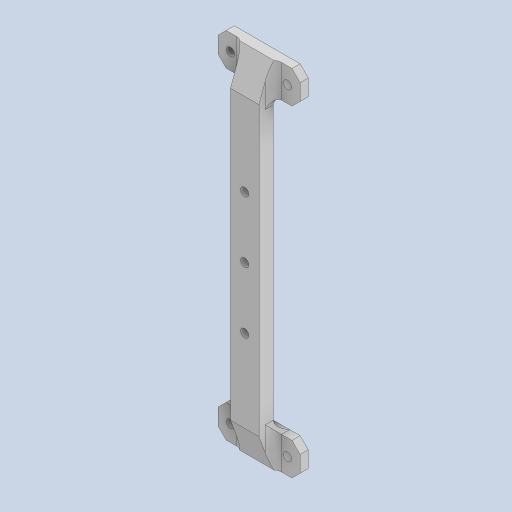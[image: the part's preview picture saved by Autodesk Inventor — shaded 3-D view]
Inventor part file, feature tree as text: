
AUTODESK INVENTOR PART (.ipt)
format: ipt  version: 2023 (Build 270158000, 158)  size: 194,560 bytes
history: native  units: mm
features: other x6, extrude x3, chamfer x3, sketch x3, projected_geometry x3, fillet x2, reference x2
ambient origin geometry x8: Origin, YZ Plane, XZ Plane, XY Plane, X Axis, Y Axis, Z Axis, Center Point
bodies: Solid1 (feature_tree)
feature tree (22):
  extrude  "Extrusion1"  Depth=2.0mm
  extrude  "Extrusion2"  Depth=2.0mm
  fillet  "Fillet1"  Radius=2.0mm
  fillet  "Fillet2"  Radius=7.0mm
  chamfer  "Chamfer1"  Distance=3.5mm
  chamfer  "Chamfer2"  Distance=2.0mm
  chamfer  "Chamfer3"  Distance=2.0mm
  extrude  "Extrusion3"  Depth=2.0mm TaperAngle=45.0deg
  sketch  "Sketch1"  dims[d0=2.0mm d1=2.0mm]
  reference  "Reference1"
  reference  "Reference2"
  sketch  "Sketch2"  dims[d2=2.0mm d3=2.0mm d4=2.0mm d5=0.0mm d6=7.0mm]
  projected_geometry  "Projected Loop1"
  projected_geometry  "Projected Loop2"
  sketch  "Sketch3"  dims[d7=87.0mm d8=3.5mm d9=0.0mm d10=2.0mm d11=2.0mm d12=2.0mm d13=2.0mm d14=45.0deg d15=3.0mm d16=2.0mm d17=12.217305mm d18=3.0mm d19=2.0mm d20=12.217305mm d21=2.0mm d22=15.0mm d23=2.0mm d24=15.0mm d25=2.0mm d26=3.5mm d27=0.0mm]
  projected_geometry  "Projected Loop3"
  parser-record x1  (decoder bookkeeping rows leaked as tree rows — omitted from the tree; the rows remain in map.json)
  other  "body_8d_1.iam"
  other  "leg_1_2d_MIR:1"
  other  "leg_holder_2_MIR:1"
  other  "leg_2d_1:1"
  other  "leg_holder_2:1"
note: 1 file-system path scrubbed to <path> (originals preserved in map.json)
